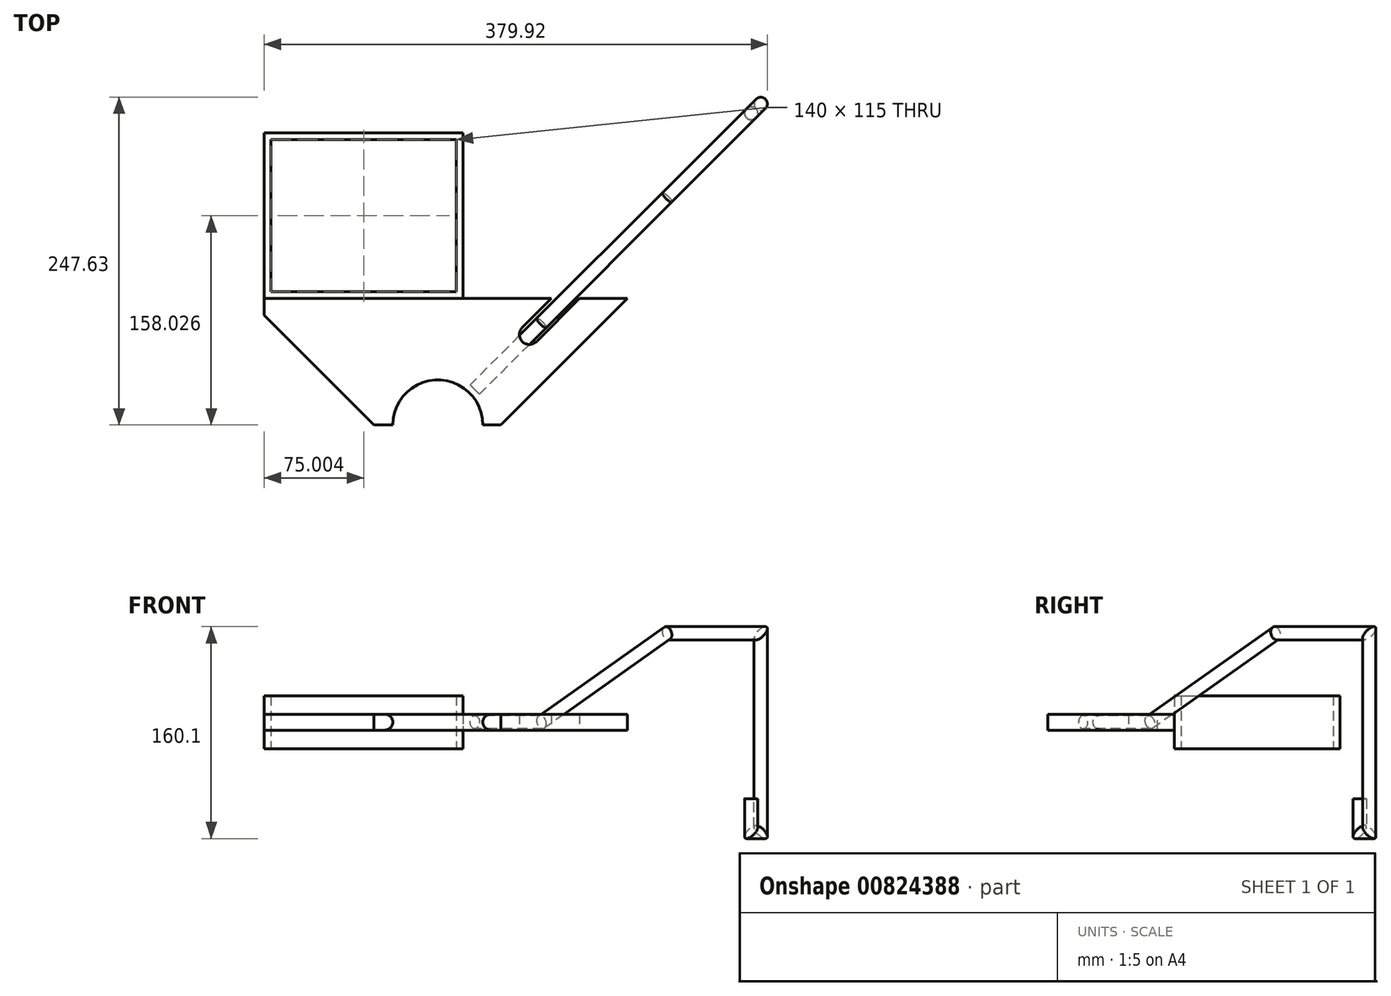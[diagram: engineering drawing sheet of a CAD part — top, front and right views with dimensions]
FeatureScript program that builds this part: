
annotation { "Feature Type Name" : "Feature", "Feature Type Description" : "" }
export const myFeature = defineFeature(function(context is Context, id is Id, definition is map)
    precondition{}
    {
        {
            var Q0;
            Q0=qCreatedBy(makeId("Front.planeOp"),FACE);
            var sketch = newSketch(context, id + "F0", { "sketchPlane" : qUnion([Q0])});
            skLineSegment(sketch, "E0", {"start": v(0, 25.44) * mm, "end": v(0, -24.32) * mm, "construction": true});
            skCircle(sketch, "E1", {"center": v(-40, 0) * mm, "radius": 6 * mm});
            skSolve(sketch);
        }
        {
            var Q0;
            Q0=sQuery(id+"F0.wireOp",EDGE,"E1");
            var Q1;
            Q1=sQuery(id+"F0.wireOp",EDGE,"E0");
            revolve(context, id + "F1", {"bodyType" : ToolBodyType.SURFACE, "surfaceOperationType" : NewSurfaceOperationType.NEW, "surfaceEntities" : qUnion([Q0]), "axis" : qUnion([Q1]), "revolveType" : RevolveType.FULL});
        }
        {
            var Q0;
            Q0=qCreatedBy(makeId("Top.planeOp"),FACE);
            var sketch = newSketch(context, id + "F2", { "sketchPlane" : qUnion([Q0])});
            skLineSegment(sketch, "E2", {"start": v(-48.15, 0) * mm, "end": v(-34, 0) * mm});
            skLineSegment(sketch, "E3", {"start": v(-48.15, 0) * mm, "end": v(-143.68, 95.53) * mm});
            skLineSegment(sketch, "E4", {"start": v(-143.68, 95.53) * mm, "end": v(85.83, 95.53) * mm});
            skLineSegment(sketch, "E5", {"start": v(143.16, 95.53) * mm, "end": v(47.63, 0) * mm});
            skArc(sketch, "E6", {"start": v(34, 0) * mm, "mid": v(0, 34) * mm, "end": v(-34, 0) * mm});
            skLineSegment(sketch, "E7.trimOffspring", {"start": v(34, 0) * mm, "end": v(47.63, 0) * mm});
            skLineSegment(sketch, "E8", {"start": v(107.04, 95.53) * mm, "end": v(74.48, 62.96) * mm});
            skLineSegment(sketch, "E9", {"start": v(85.83, 95.53) * mm, "end": v(63.87, 73.57) * mm});
            skLineSegment(sketch, "E10.trimOffspring", {"start": v(107.04, 95.53) * mm, "end": v(143.16, 95.53) * mm});
            skArc(sketch, "E11", {"start": v(74.48, 62.96) * mm, "mid": v(63.87, 62.96) * mm, "end": v(63.87, 73.57) * mm});
            skSolve(sketch);
        }
        {
            var Q0;
            Q0 = qSketchRegion(id + "F2", true);
            extrude(context, id + "F3", {"entities" : qUnion([Q0]), "depth" : 6 * mm, "offsetDistance" : 25 * mm, "hasSecondDirection" : true, "secondDirectionOppositeDirection" : true, "secondDirectionDepth" : 6 * mm});
        }
        {
            var Q0;
            Q0=makeQuery(id+"F3.opExtrude","CAP_EDGE",EDGE,{"disambiguationData":[OSD([sQuery(id+"F2.wireOp",EDGE,"E6")])],"isStart":false});
            var Q1;
            Q1=makeQuery(id+"F3.opExtrude","CAP_EDGE",EDGE,{"disambiguationData":[OSD([sQuery(id+"F2.wireOp",EDGE,"E6")])],"isStart":true});
            fillet(context, id + "F4", {"entities" : qUnion([Q0, Q1]), "radius" : 6 * mm, "tangentPropagation" : true, "allowEdgeOverflow" : false});
        }
        {
            var Q0;
            Q0=qCreatedBy(makeId("Top.planeOp"),FACE);
            var sketch = newSketch(context, id + "F5", { "sketchPlane" : qUnion([Q0])});
            skLineSegment(sketch, "E12.bottom", {"start": v(18.98, 95.53) * mm, "end": v(-131.02, 95.53) * mm});
            skLineSegment(sketch, "E12.top", {"start": v(18.98, 220.53) * mm, "end": v(-131.02, 220.53) * mm});
            skLineSegment(sketch, "E12.left", {"start": v(18.98, 95.53) * mm, "end": v(18.98, 220.53) * mm});
            skLineSegment(sketch, "E12.right", {"start": v(-131.02, 95.53) * mm, "end": v(-131.02, 220.53) * mm});
            skLineSegment(sketch, "E13.bottom", {"start": v(13.98, 100.53) * mm, "end": v(-126.02, 100.53) * mm});
            skLineSegment(sketch, "E13.left", {"start": v(13.98, 100.53) * mm, "end": v(13.98, 215.53) * mm});
            skLineSegment(sketch, "E13.right", {"start": v(-126.02, 100.53) * mm, "end": v(-126.02, 215.53) * mm});
            skLineSegment(sketch, "E14", {"start": v(13.98, 215.53) * mm, "end": v(-126.02, 215.53) * mm});
            skSolve(sketch);
        }
        {
            var Q0;
            Q0 = qSketchRegion(id + "F5", true);
            extrude(context, id + "F6", {"entities" : qUnion([Q0]), "operationType" : NewBodyOperationType.ADD, "depth" : 20 * mm, "offsetDistance" : 25 * mm, "hasSecondDirection" : true, "secondDirectionOppositeDirection" : true, "secondDirectionDepth" : 20 * mm});
        }
        {
            var Q0;
            Q0=qCreatedBy(makeId("Top.planeOp"),FACE);
            var sketch = newSketch(context, id + "F7", { "sketchPlane" : qUnion([Q0])});
            skLineSegment(sketch, "E15.bottom", {"start": v(-131.02, 97.53) * mm, "end": v(-149.44, 97.53) * mm});
            skLineSegment(sketch, "E15.top", {"start": v(-131.02, 74.9) * mm, "end": v(-149.44, 74.9) * mm});
            skLineSegment(sketch, "E15.left", {"start": v(-131.02, 97.53) * mm, "end": v(-131.02, 74.9) * mm});
            skLineSegment(sketch, "E15.right", {"start": v(-149.44, 97.53) * mm, "end": v(-149.44, 74.9) * mm});
            skSolve(sketch);
        }
        {
            var Q0;
            Q0 = qSketchRegion(id + "F7", true);
            extrude(context, id + "F8", {"entities" : qUnion([Q0]), "operationType" : NewBodyOperationType.REMOVE, "depth" : 25 * mm, "offsetDistance" : 25 * mm, "hasSecondDirection" : true, "secondDirectionOppositeDirection" : true, "secondDirectionDepth" : 25 * mm});
        }
        {
            var Q0;
            Q0=makeQuery(id+"F3.opExtrude","SWEPT_FACE",FACE,{"disambiguationData":[OSD([sQuery(id+"F2.wireOp",EDGE,"E9")])]});
            cPlane(context, id + "F9", {"entities" : qUnion([Q0]), "cplaneType" : CPlaneType.OFFSET, "offset" : 7.5 * mm, "width" : 150 * mm, "height" : 150 * mm});
        }
        {
            var Q0;
            Q0=qCreatedBy(id+"F9.planeOp",FACE);
            var sketch = newSketch(context, id + "F10", { "sketchPlane" : qUnion([Q0])});
            skLineSegment(sketch, "E16", {"start": v(109.83, 0) * mm, "end": v(243.98, 67.1) * mm});
            skLineSegment(sketch, "E17", {"start": v(243.98, 67.1) * mm, "end": v(343.98, 67.1) * mm});
            skLineSegment(sketch, "E18", {"start": v(343.98, 67.1) * mm, "end": v(343.98, -82.9) * mm});
            skLineSegment(sketch, "E19", {"start": v(109.83, 0) * mm, "end": v(88.65, 0) * mm});
            skLineSegment(sketch, "E20", {"start": v(343.98, -82.9) * mm, "end": v(333.98, -82.9) * mm});
            skLineSegment(sketch, "E21", {"start": v(333.98, -82.9) * mm, "end": v(333.98, -57.9) * mm});
            skPoint(sketch, "E22.end.orphan", {"position": v(0, 0) * mm});
            skLineSegment(sketch, "E23", {"start": v(88.65, 0) * mm, "end": v(38.64, 0) * mm});
            skSolve(sketch);
        }
        {
            var Q0;
            Q0=makeQuery(id+"F3.opExtrude","CAP_FACE",FACE,{"disambiguationData":[OSD([sQuery(id+"F2.wireOp",EDGE,"E2"),sQuery(id+"F2.wireOp",EDGE,"E3"),sQuery(id+"F2.wireOp",EDGE,"E4"),sQuery(id+"F2.wireOp",EDGE,"E5"),sQuery(id+"F2.wireOp",EDGE,"E6"),sQuery(id+"F2.wireOp",EDGE,"E7.trimOffspring"),sQuery(id+"F2.wireOp",EDGE,"E8"),sQuery(id+"F2.wireOp",EDGE,"E9"),sQuery(id+"F2.wireOp",EDGE,"E10.trimOffspring"),sQuery(id+"F2.wireOp",EDGE,"E11")])],"isStart":false});
            var Q1;
            Q1=sQuery(id+"F10.wireOp",VERTEX,"E21.end");
            cPlane(context, id + "F11", {"entities" : qUnion([Q0, Q1]), "cplaneType" : CPlaneType.PLANE_POINT, "offset" : 25 * mm, "width" : 150 * mm, "height" : 150 * mm});
        }
        {
            var Q0;
            Q0=qCreatedBy(id+"F11.planeOp",FACE);
            var sketch = newSketch(context, id + "F12", { "sketchPlane" : qUnion([Q0])});
            skCircle(sketch, "E24", {"center": v(236.76, 235.49) * mm, "radius": 5 * mm});
            skSolve(sketch);
        }
        {
            var Q0;
            Q0=makeQuery(id+"F12.imprint","IMPRINT",FACE,{"disambiguationData":[TD([[makeQuery(id+"F12.imprint","IMPRINT",EDGE,{"derivedFrom":sQuery(id+"F12.wireOp",EDGE,"E24")}),1.0]])]});
            var Q1;
            Q1=sQuery(id+"F10.wireOp",EDGE,"E21");
            var Q2;
            Q2=sQuery(id+"F10.wireOp",EDGE,"E20");
            var Q3;
            Q3=sQuery(id+"F10.wireOp",EDGE,"E18");
            var Q4;
            Q4=sQuery(id+"F10.wireOp",EDGE,"E17");
            var Q5;
            Q5=sQuery(id+"F10.wireOp",EDGE,"E16");
            var Q6;
            Q6=sQuery(id+"F10.wireOp",EDGE,"E19");
            var Q7;
            Q7=sQuery(id+"F10.wireOp",EDGE,"E23");
            sweep(context, id + "F13", {"profiles" : qUnion([Q0]), "path" : qUnion([Q1, Q2, Q3, Q4, Q5, Q6, Q7])});
        }
    });
